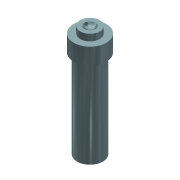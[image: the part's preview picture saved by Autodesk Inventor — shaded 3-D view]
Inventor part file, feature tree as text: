
AUTODESK INVENTOR PART (.ipt)
format: ipt  version: 2022.1 (Build 261234020, 234B)  size: 141,824 bytes
history: native  units: mm
features: sketch x10, extrude x10, revolve x1
ambient origin geometry x8: Origin, YZ Plane, XZ Plane, XY Plane, X Axis, Y Axis, Z Axis, Center Point
bodies: Solid1 (feature_tree)
feature tree (21):
  sketch  "Sketch1"  dims[d0=4.0mm d1=6.0mm]
  extrude  "Extrusion1"  Depth=6.0mm
  revolve  "Revolution1"  Angle=90.0deg
  extrude  "Extrusion2"  Depth=10.0mm
  extrude  "Extrusion3"  Depth=5.0mm TaperAngle=0.0deg
  extrude  "Extrusion4"  Depth=25.0mm TaperAngle=0.0deg
  extrude  "Extrusion5"  Depth=0.1mm TaperAngle=0.0deg
  extrude  "Extrusion6"  Depth=2.0mm TaperAngle=0.0deg
  extrude  "Extrusion7"  [1 undecoded]
  extrude  "Extrusion8"  [1 undecoded]
  extrude  "Extrusion9"  [1 undecoded]
  extrude  "Extrusion10"  [1 undecoded]
  sketch  "Sketch2"  dims[d2=15.0mm d3=0.0mm d4=90.0deg]
  sketch  "Sketch3"  dims[d5=1.1mm d6=0.0mm d7=10.0mm]
  sketch  "Sketch4"  dims[d8=10.0mm d9=0.0mm d10=5.0mm d11=0.0mm]
  sketch  "Sketch5"  dims[d12=7.9mm d13=25.0mm d14=0.0mm]
  sketch  "Sketch6"  dims[d15=0.1mm d16=0.0mm d17=0.1mm d18=0.0mm]
  sketch  "Sketch7"  dims[d19=0.1mm d20=0.0mm d21=2.0mm d22=0.0mm]
  sketch  "Sketch8"  dims[d23=2.0mm d24=0.0mm]
  sketch  "Sketch9"
  sketch  "Sketch10"
note: 4 required parameter values undecoded (feature->parameter linkage not recoverable at this tier; creation-order binding heuristic only, values carry confidence <= 0.55)
